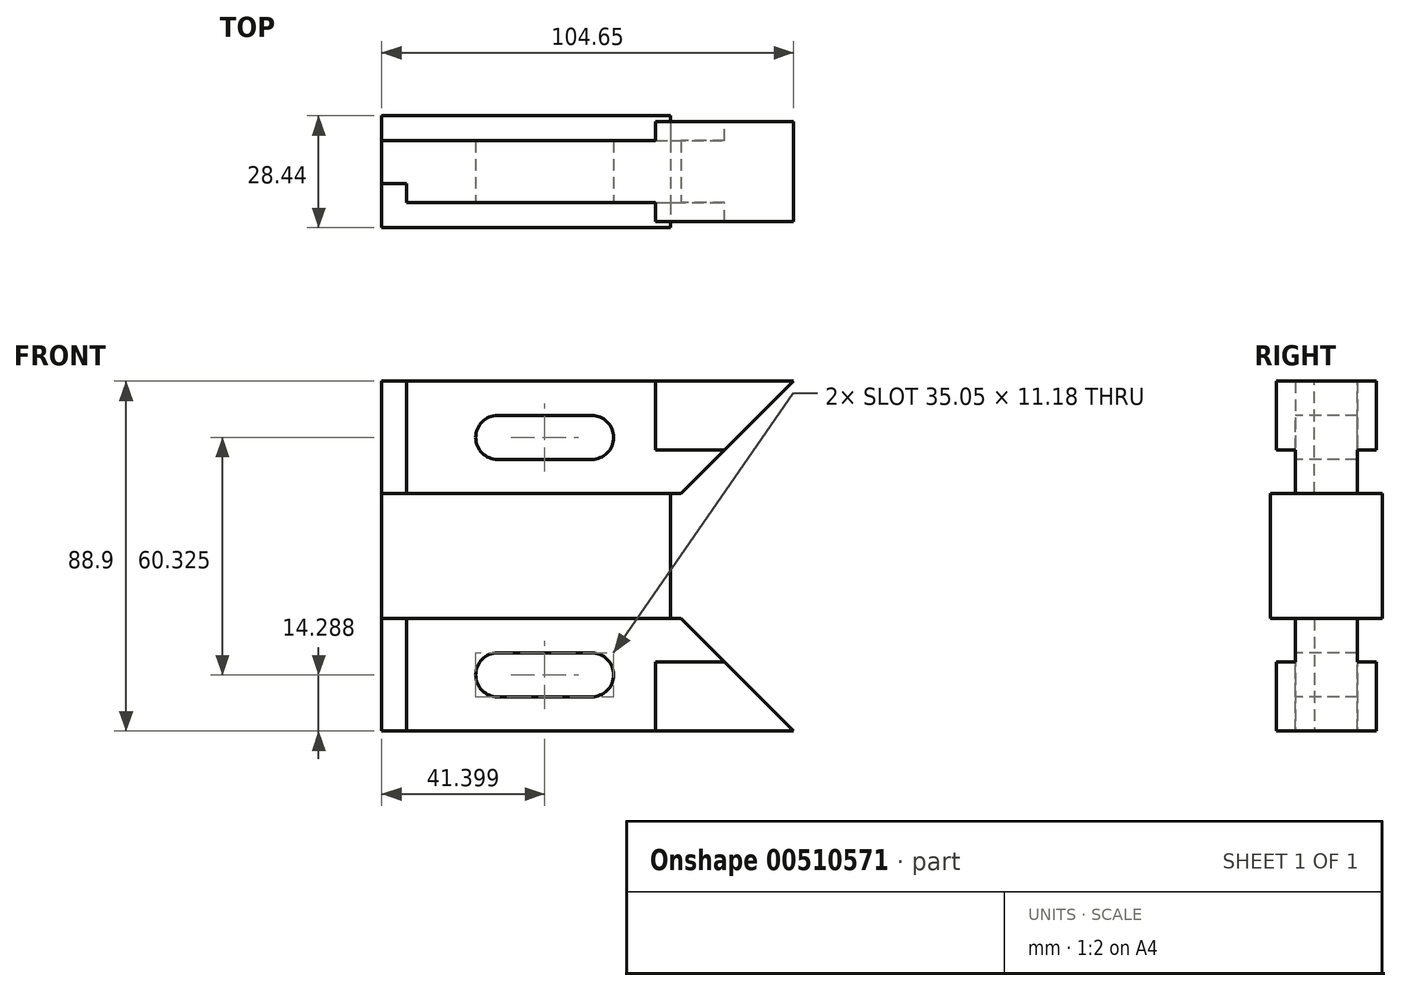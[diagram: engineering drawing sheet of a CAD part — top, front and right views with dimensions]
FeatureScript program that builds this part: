
annotation { "Feature Type Name" : "Feature", "Feature Type Description" : "" }
export const myFeature = defineFeature(function(context is Context, id is Id, definition is map)
    precondition{}
    {
        {
            var Q0;
            Q0=qCreatedBy(makeId("Front.planeOp"),FACE);
            var sketch = newSketch(context, id + "F0", { "sketchPlane" : qUnion([Q0])});
            skLineSegment(sketch, "E0.bottom", {"start": v(-36.7, 15.88) * mm, "end": v(36.7, 15.88) * mm});
            skLineSegment(sketch, "E0.top", {"start": v(-36.7, -15.88) * mm, "end": v(36.7, -15.88) * mm});
            skLineSegment(sketch, "E0.left", {"start": v(-36.7, 15.88) * mm, "end": v(-36.7, -15.88) * mm});
            skLineSegment(sketch, "E0.right", {"start": v(36.7, 15.88) * mm, "end": v(36.7, -15.88) * mm});
            skPoint(sketch, "E0.middle", {"position": v(0, 0) * mm});
            skLineSegment(sketch, "E1", {"start": v(-36.7, 15.88) * mm, "end": v(-36.7, 44.45) * mm});
            skLineSegment(sketch, "E2", {"start": v(-36.7, 44.45) * mm, "end": v(67.95, 44.45) * mm});
            skLineSegment(sketch, "E3", {"start": v(67.95, 44.45) * mm, "end": v(39.37, 15.87) * mm});
            skLineSegment(sketch, "E4.MirrorCS", {"start": v(-36.7, -15.88) * mm, "end": v(-36.7, -44.45) * mm});
            skLineSegment(sketch, "E5.MirrorCS", {"start": v(-36.7, -44.45) * mm, "end": v(67.95, -44.45) * mm});
            skLineSegment(sketch, "E6.MirrorCS", {"start": v(67.95, -44.45) * mm, "end": v(39.37, -15.87) * mm});
            skPoint(sketch, "E7.end.orphan", {"position": v(36.7, -15.88) * mm});
            skLineSegment(sketch, "E8", {"start": v(36.7, 15.88) * mm, "end": v(39.37, 15.88) * mm});
            skLineSegment(sketch, "E9", {"start": v(39.37, -15.88) * mm, "end": v(36.7, -15.88) * mm});
            skSolve(sketch);
        }
        {
            var Q0;
            Q0=qCreatedBy(makeId("Front.planeOp"),FACE);
            var sketch = newSketch(context, id + "F1", { "sketchPlane" : qUnion([Q0])});
            skLineSegment(sketch, "E10.bottom", {"start": v(16.64, 35.75) * mm, "end": v(-7.24, 35.75) * mm});
            skLineSegment(sketch, "E10.top", {"start": v(16.64, 24.57) * mm, "end": v(-7.24, 24.57) * mm});
            skPoint(sketch, "E10.middle", {"position": v(4.7, 30.16) * mm});
            skArc(sketch, "E11", {"start": v(-7.24, 35.75) * mm, "mid": v(-12.83, 30.16) * mm, "end": v(-7.24, 24.57) * mm});
            skArc(sketch, "E12", {"start": v(16.64, 24.57) * mm, "mid": v(22.22, 30.16) * mm, "end": v(16.64, 35.75) * mm});
            skLineSegment(sketch, "E13.MirrorCS", {"start": v(16.64, -35.75) * mm, "end": v(-7.24, -35.75) * mm});
            skLineSegment(sketch, "E14.MirrorCS", {"start": v(16.64, -24.57) * mm, "end": v(-7.24, -24.57) * mm});
            skArc(sketch, "E15.MirrorCS", {"start": v(16.64, -24.57) * mm, "mid": v(22.22, -30.16) * mm, "end": v(16.64, -35.75) * mm});
            skPoint(sketch, "E16.MirrorP", {"position": v(4.7, -30.16) * mm});
            skArc(sketch, "E17.MirrorCS", {"start": v(-7.24, -35.75) * mm, "mid": v(-12.83, -30.16) * mm, "end": v(-7.24, -24.57) * mm});
            skCircle(sketch, "E18", {"center": v(-7.24, -30.16) * mm, "radius": 14.29 * mm, "construction": true});
            skCircle(sketch, "E19.MirrorC", {"center": v(-7.24, 30.16) * mm, "radius": 14.29 * mm, "construction": true});
            skPoint(sketch, "E20.orphan", {"position": v(11.12, 29.27) * mm});
            skPoint(sketch, "E21.orphan", {"position": v(11.12, -29.27) * mm});
            skSolve(sketch);
        }
        {
            var Q0;
            Q0=qCreatedBy(makeId("Front.planeOp"),FACE);
            var sketch = newSketch(context, id + "F2", { "sketchPlane" : qUnion([Q0])});
            skLineSegment(sketch, "E22.0", {"start": v(32.9, 44.45) * mm, "end": v(67.95, 44.45) * mm});
            skLineSegment(sketch, "E23.0", {"start": v(67.95, 44.45) * mm, "end": v(50.42, 26.92) * mm});
            skLineSegment(sketch, "E24.0", {"start": v(67.95, -44.45) * mm, "end": v(50.42, -26.92) * mm});
            skLineSegment(sketch, "E25.0", {"start": v(32.9, -44.45) * mm, "end": v(67.95, -44.45) * mm});
            skLineSegment(sketch, "E26", {"start": v(32.9, 44.45) * mm, "end": v(32.9, 26.92) * mm});
            skLineSegment(sketch, "E27", {"start": v(32.9, 26.92) * mm, "end": v(50.42, 26.92) * mm});
            skLineSegment(sketch, "E28.MirrorCS", {"start": v(32.9, -44.45) * mm, "end": v(32.9, -26.92) * mm});
            skLineSegment(sketch, "E29.MirrorCS", {"start": v(32.9, -26.92) * mm, "end": v(50.42, -26.92) * mm});
            skPoint(sketch, "E30.orphan", {"position": v(-36.7, 44.45) * mm});
            skPoint(sketch, "E31.orphan", {"position": v(39.37, 15.87) * mm});
            skPoint(sketch, "E32.orphan", {"position": v(39.37, -15.87) * mm});
            skPoint(sketch, "E33.orphan", {"position": v(-36.7, -44.45) * mm});
            skSolve(sketch);
        }
        {
            var Q0;
            Q0=qCreatedBy(makeId("Right.planeOp"),FACE);
            var sketch = newSketch(context, id + "F3", { "sketchPlane" : qUnion([Q0])});
            skLineSegment(sketch, "E34.bottom", {"start": v(14.22, 15.88) * mm, "end": v(-14.22, 15.88) * mm});
            skLineSegment(sketch, "E34.top", {"start": v(14.22, -15.88) * mm, "end": v(-14.22, -15.88) * mm});
            skLineSegment(sketch, "E34.left", {"start": v(14.22, 15.88) * mm, "end": v(14.22, -15.88) * mm});
            skLineSegment(sketch, "E34.right", {"start": v(-14.22, 15.88) * mm, "end": v(-14.22, -15.88) * mm});
            skPoint(sketch, "E34.middle", {"position": v(0, 0) * mm});
            skLineSegment(sketch, "E35.bottom", {"start": v(12.7, 44.45) * mm, "end": v(-12.7, 44.45) * mm});
            skLineSegment(sketch, "E35.top", {"start": v(12.7, 26.92) * mm, "end": v(-12.7, 26.92) * mm});
            skLineSegment(sketch, "E35.left", {"start": v(12.7, 44.45) * mm, "end": v(12.7, 26.92) * mm});
            skLineSegment(sketch, "E35.right", {"start": v(-12.7, 44.45) * mm, "end": v(-12.7, 26.92) * mm});
            skPoint(sketch, "E35.middle", {"position": v(0, 35.69) * mm});
            skLineSegment(sketch, "E36", {"start": v(-7.87, 44.45) * mm, "end": v(-7.87, 15.88) * mm});
            skLineSegment(sketch, "E37", {"start": v(-3.05, 44.45) * mm, "end": v(-3.05, 15.88) * mm});
            skLineSegment(sketch, "E38.MirrorCS", {"start": v(7.87, 44.45) * mm, "end": v(7.87, 15.88) * mm});
            skSolve(sketch);
        }
        {
            var Q0;
            Q0=sQuery(id+"F3.wireOp",EDGE,"E37");
            cPlane(context, id + "F4", {"entities" : qUnion([Q0]), "cplaneType" : CPlaneType.LINE_ANGLE, "offset" : 25.4 * mm, "angle" : 90 * degree, "oppositeDirection" : true, "width" : 152.4 * mm, "height" : 152.4 * mm});
        }
        {
            var Q0;
            Q0=qCreatedBy(id+"F4.planeOp",FACE);
            var sketch = newSketch(context, id + "F5", { "sketchPlane" : qUnion([Q0])});
            skLineSegment(sketch, "E39.0", {"start": v(-36.7, 15.88) * mm, "end": v(-36.7, 44.45) * mm});
            skLineSegment(sketch, "E40.0", {"start": v(-36.7, 44.45) * mm, "end": v(-30.35, 44.45) * mm});
            skLineSegment(sketch, "E41.0", {"start": v(-36.7, 15.88) * mm, "end": v(-30.35, 15.88) * mm});
            skLineSegment(sketch, "E42.0", {"start": v(-36.7, -15.88) * mm, "end": v(-30.35, -15.88) * mm});
            skLineSegment(sketch, "E43.0", {"start": v(-36.7, -15.88) * mm, "end": v(-36.7, -44.45) * mm});
            skLineSegment(sketch, "E44.0", {"start": v(-36.7, -44.45) * mm, "end": v(-30.35, -44.45) * mm});
            skLineSegment(sketch, "E45", {"start": v(-30.35, 44.45) * mm, "end": v(-30.35, 15.88) * mm});
            skPoint(sketch, "E46.orphan", {"position": v(67.95, 44.45) * mm});
            skPoint(sketch, "E47.orphan", {"position": v(36.7, 15.88) * mm});
            skLineSegment(sketch, "E48.trimOffspring", {"start": v(-30.35, -15.88) * mm, "end": v(-30.35, -44.45) * mm});
            skPoint(sketch, "E49.orphan", {"position": v(36.7, -15.88) * mm});
            skPoint(sketch, "E50.orphan", {"position": v(67.95, -44.45) * mm});
            skSolve(sketch);
        }
        {
            var Q0;
            Q0=makeQuery(id+"F0.imprint","IMPRINT",FACE,{"disambiguationData":[TD([[makeQuery(id+"F0.imprint","IMPRINT",EDGE,{"derivedFrom":sQuery(id+"F0.wireOp",EDGE,"E0.bottom")}),-1.0]])]});
            var Q1;
            Q1=sQuery(id+"F3.wireOp",VERTEX,"E34.left.start");
            var Q2;
            Q2=sQuery(id+"F3.wireOp",VERTEX,"E34.top.end");
            extrude(context, id + "F6", {"entities" : qUnion([Q0]), "endBound" : BoundingType.UP_TO_VERTEX, "oppositeDirection" : true, "depth" : 25.4 * mm, "endBoundEntityVertex" : qUnion([Q1]), "offsetDistance" : 25.4 * mm, "hasSecondDirection" : true, "secondDirectionBound" : SecondDirectionBoundingType.UP_TO_VERTEX, "secondDirectionOppositeDirection" : false, "secondDirectionDepth" : 25.4 * mm, "secondDirectionBoundEntityVertex" : qUnion([Q2])});
        }
        {
            var Q0;
            Q0=makeQuery(id+"F0.imprint","IMPRINT",FACE,{"disambiguationData":[TD([[makeQuery(id+"F0.imprint","IMPRINT",EDGE,{"derivedFrom":sQuery(id+"F0.wireOp",EDGE,"E0.bottom")}),1.0]])]});
            var Q1;
            Q1=makeQuery(id+"F0.imprint","IMPRINT",FACE,{"disambiguationData":[TD([[makeQuery(id+"F0.imprint","IMPRINT",EDGE,{"derivedFrom":sQuery(id+"F0.wireOp",EDGE,"E0.top")}),-1.0]])]});
            var Q2;
            Q2=sQuery(id+"F3.wireOp",VERTEX,"E38.MirrorCS.start");
            var Q3;
            Q3=sQuery(id+"F3.wireOp",VERTEX,"E36.start");
            extrude(context, id + "F7", {"entities" : qUnion([Q0, Q1]), "operationType" : NewBodyOperationType.ADD, "endBound" : BoundingType.UP_TO_VERTEX, "oppositeDirection" : true, "depth" : 25.4 * mm, "endBoundEntityVertex" : qUnion([Q2]), "offsetDistance" : 25.4 * mm, "hasSecondDirection" : true, "secondDirectionBound" : SecondDirectionBoundingType.UP_TO_VERTEX, "secondDirectionOppositeDirection" : false, "secondDirectionDepth" : 25.4 * mm, "secondDirectionBoundEntityVertex" : qUnion([Q3])});
        }
        {
            var Q0;
            Q0=makeQuery(id+"F1.imprint","IMPRINT",FACE,{"disambiguationData":[TD([[makeQuery(id+"F1.imprint","IMPRINT",EDGE,{"derivedFrom":sQuery(id+"F1.wireOp",EDGE,"E10.bottom")}),1.0]])]});
            var Q1;
            Q1=makeQuery(id+"F1.imprint","IMPRINT",FACE,{"disambiguationData":[TD([[makeQuery(id+"F1.imprint","IMPRINT",EDGE,{"derivedFrom":sQuery(id+"F1.wireOp",EDGE,"E13.MirrorCS")}),-1.0]])]});
            extrude(context, id + "F8", {"entities" : qUnion([Q0, Q1]), "operationType" : NewBodyOperationType.REMOVE, "endBound" : BoundingType.SYMMETRIC, "oppositeDirection" : true, "depth" : 25.4 * mm, "offsetDistance" : 25.4 * mm});
        }
        {
            var Q0;
            Q0=makeQuery(id+"F2.imprint","IMPRINT",FACE,{"disambiguationData":[TD([[makeQuery(id+"F2.imprint","IMPRINT",EDGE,{"derivedFrom":sQuery(id+"F2.wireOp",EDGE,"E22.0")}),-1.0]])]});
            var Q1;
            Q1=makeQuery(id+"F2.imprint","IMPRINT",FACE,{"disambiguationData":[TD([[makeQuery(id+"F2.imprint","IMPRINT",EDGE,{"derivedFrom":sQuery(id+"F2.wireOp",EDGE,"E24.0")}),1.0]])]});
            var Q2;
            Q2=sQuery(id+"F3.wireOp",VERTEX,"E35.bottom.end");
            var Q3;
            Q3=sQuery(id+"F3.wireOp",VERTEX,"E35.left.start");
            extrude(context, id + "F9", {"entities" : qUnion([Q0, Q1]), "operationType" : NewBodyOperationType.ADD, "endBound" : BoundingType.UP_TO_VERTEX, "depth" : 25.4 * mm, "endBoundEntityVertex" : qUnion([Q2]), "offsetDistance" : 25.4 * mm, "hasSecondDirection" : true, "secondDirectionBound" : SecondDirectionBoundingType.UP_TO_VERTEX, "secondDirectionOppositeDirection" : true, "secondDirectionDepth" : 25.4 * mm, "secondDirectionBoundEntityVertex" : qUnion([Q3])});
        }
        {
            var Q0;
            Q0=makeQuery(id+"F5.imprint","IMPRINT",FACE,{"disambiguationData":[TD([[makeQuery(id+"F5.imprint","IMPRINT",EDGE,{"derivedFrom":sQuery(id+"F5.wireOp",EDGE,"E42.0")}),-1.0]])]});
            var Q1;
            Q1=makeQuery(id+"F5.imprint","IMPRINT",FACE,{"disambiguationData":[TD([[makeQuery(id+"F5.imprint","IMPRINT",EDGE,{"derivedFrom":sQuery(id+"F5.wireOp",EDGE,"E39.0")}),-1.0]])]});
            extrude(context, id + "F10", {"entities" : qUnion([Q0, Q1]), "operationType" : NewBodyOperationType.REMOVE, "depth" : 25.4 * mm, "offsetDistance" : 25.4 * mm});
        }
        {
            var Q0;
            Q0=makeQuery(id+"F0.imprint","IMPRINT",FACE,{"disambiguationData":[TD([[makeQuery(id+"F0.imprint","IMPRINT",EDGE,{"derivedFrom":sQuery(id+"F0.wireOp",EDGE,"E0.bottom")}),-1.0]])]});
            var Q1;
            Q1=sQuery(id+"F3.wireOp",VERTEX,"E34.right.end");
            var Q2;
            Q2=sQuery(id+"F3.wireOp",VERTEX,"E34.left.start");
            extrude(context, id + "F11", {"entities" : qUnion([Q0]), "endBound" : BoundingType.UP_TO_VERTEX, "endBoundEntityVertex" : qUnion([Q1]), "depth" : 25.4 * mm, "hasSecondDirection" : true, "secondDirectionBound" : SecondDirectionBoundingType.UP_TO_VERTEX, "secondDirectionOppositeDirection" : true, "secondDirectionBoundEntityVertex" : qUnion([Q2]), "secondDirectionDepth" : 25.4 * mm});
        }
        {
            var Q0;
            Q0=makeQuery(id+"F0.imprint","IMPRINT",FACE,{"disambiguationData":[TD([[makeQuery(id+"F0.imprint","IMPRINT",EDGE,{"derivedFrom":sQuery(id+"F0.wireOp",EDGE,"E0.bottom")}),1.0]])]});
            var Q1;
            Q1=makeQuery(id+"F0.imprint","IMPRINT",FACE,{"disambiguationData":[TD([[makeQuery(id+"F0.imprint","IMPRINT",EDGE,{"derivedFrom":sQuery(id+"F0.wireOp",EDGE,"E0.top")}),-1.0]])]});
            var Q2;
            Q2=sQuery(id+"F3.wireOp",VERTEX,"E36.start");
            var Q3;
            Q3=sQuery(id+"F3.wireOp",VERTEX,"E38.MirrorCS.start");
            extrude(context, id + "F12", {"entities" : qUnion([Q0, Q1]), "operationType" : NewBodyOperationType.ADD, "endBound" : BoundingType.UP_TO_VERTEX, "endBoundEntityVertex" : qUnion([Q2]), "depth" : 25.4 * mm, "hasSecondDirection" : true, "secondDirectionBound" : SecondDirectionBoundingType.UP_TO_VERTEX, "secondDirectionOppositeDirection" : true, "secondDirectionBoundEntityVertex" : qUnion([Q3]), "secondDirectionDepth" : 25.4 * mm});
        }
        {
            var Q0;
            Q0=qSketchRegion(id+"F1",true);
            var Q1;
            Q1=sQuery(id+"F3.wireOp",VERTEX,"E35.left.start");
            var Q2;
            Q2=sQuery(id+"F3.wireOp",VERTEX,"E35.bottom.end");
            extrude(context, id + "F13", {"entities" : qUnion([Q0]), "operationType" : NewBodyOperationType.REMOVE, "endBound" : BoundingType.UP_TO_VERTEX, "oppositeDirection" : true, "endBoundEntityVertex" : qUnion([Q1]), "depth" : 25.4 * mm, "hasSecondDirection" : true, "secondDirectionBound" : SecondDirectionBoundingType.UP_TO_VERTEX, "secondDirectionOppositeDirection" : false, "secondDirectionBoundEntityVertex" : qUnion([Q2]), "secondDirectionDepth" : 25.4 * mm});
        }
        {
            var Q0;
            Q0=qSketchRegion(id+"F2",true);
            var Q1;
            Q1=sQuery(id+"F3.wireOp",VERTEX,"E35.bottom.end");
            var Q2;
            Q2=sQuery(id+"F3.wireOp",VERTEX,"E35.left.start");
            extrude(context, id + "F14", {"entities" : qUnion([Q0]), "operationType" : NewBodyOperationType.ADD, "endBound" : BoundingType.UP_TO_VERTEX, "endBoundEntityVertex" : qUnion([Q1]), "depth" : 25.4 * mm, "hasSecondDirection" : true, "secondDirectionBound" : SecondDirectionBoundingType.UP_TO_VERTEX, "secondDirectionOppositeDirection" : true, "secondDirectionBoundEntityVertex" : qUnion([Q2]), "secondDirectionDepth" : 25.4 * mm});
        }
        {
            var Q0;
            Q0=qSketchRegion(id+"F5",true);
            var Q1;
            Q1=sQuery(id+"F3.wireOp",VERTEX,"E35.bottom.end");
            var Q2;
            Q2=sQuery(id+"F3.wireOp",VERTEX,"E37.start");
            extrude(context, id + "F15", {"entities" : qUnion([Q0]), "operationType" : NewBodyOperationType.REMOVE, "endBound" : BoundingType.UP_TO_VERTEX, "endBoundEntityVertex" : qUnion([Q1]), "depth" : 25.4 * mm});
        }
    });
